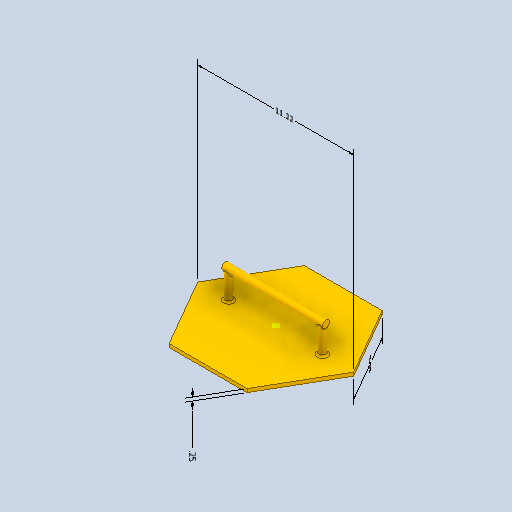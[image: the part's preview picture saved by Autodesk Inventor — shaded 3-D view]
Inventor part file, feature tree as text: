
AUTODESK INVENTOR PART (.ipt)
format: ipt  version: 2022 (Build 260153000, 153)  size: 196,096 bytes
history: native  units: in
note: dims shown in document units (in); Inventor stores cm internally (conversion verified against a paired STEP export)
features: other x4, sketch x4, extrude x3, fillet x1
ambient origin geometry x8: Origin, YZ Plane, XZ Plane, XY Plane, X Axis, Y Axis, Z Axis, Center Point
bodies: Solid1 (feature_tree)
feature tree (12):
  other  "Annotations"
  extrude  "Extrusion1"  Depth=1.0in
  sketch  "Sketch2"  dims[d2=0.125in d3=0.25in d4=0.0in]
  extrude  "Extrusion2"  Depth=0.25in TaperAngle=0.0deg
  extrude  "Extrusion3"  Depth=0.5in
  fillet  "Fillet2"  Radius=6.75in
  sketch  "Sketch1"  dims[d0=7.5in d1=1.0in]
  sketch  "Sketch3"  dims[d15=10.9697in d16=0.5in d17=6.75in]
  sketch  "Sketch4"  dims[d18=3.375in d19=2.0in d20=0.0in d21=7.25in d22=0.0in d24=0.125in d10=0.1768in d11=0.25in d12=0.2952in d13=0.3376in d14=11.2197in d6=0.2098in d7=0.199in d8=5.6098in d9=0.1556in]
  other  "Linear Dimension 1"
  other  "Linear Dimension 2"
  other  "Linear Dimension 3"
